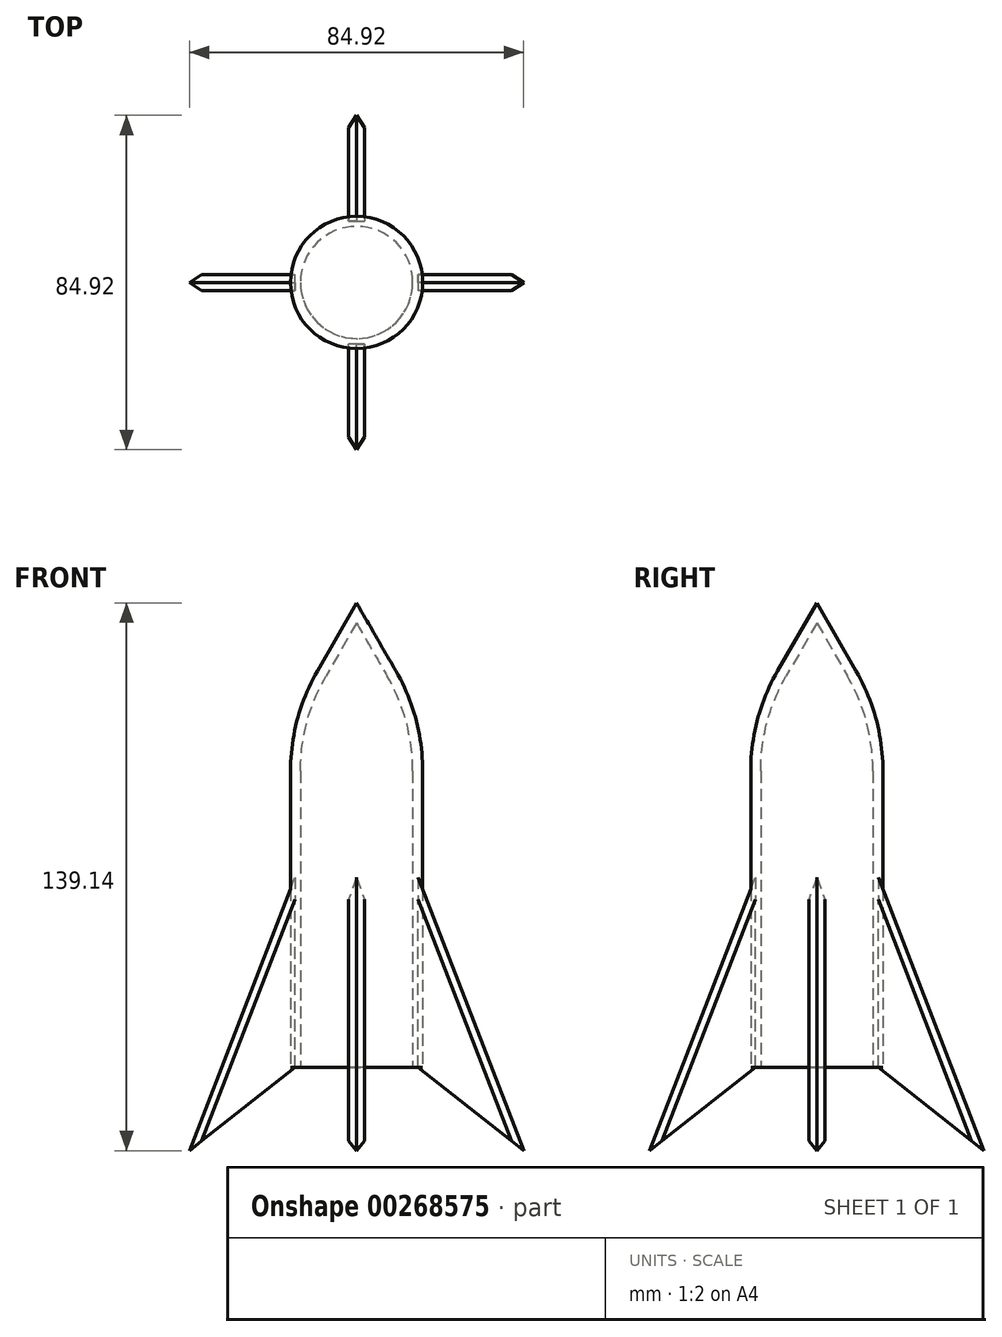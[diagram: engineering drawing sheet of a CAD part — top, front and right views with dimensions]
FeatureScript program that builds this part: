
annotation { "Feature Type Name" : "Feature", "Feature Type Description" : "" }
export const myFeature = defineFeature(function(context is Context, id is Id, definition is map)
    precondition{}
    {
        {
            var Q0;
            Q0=qCreatedBy(makeId("Top.planeOp"),FACE);
            var sketch = newSketch(context, id + "F0", { "sketchPlane" : qUnion([Q0])});
            skCircle(sketch, "E0", {"center": v(0, 0) * mm, "radius": 16.8 * mm});
            skSolve(sketch);
        }
        {
            var Q0;
            Q0=makeQuery(id+"F0.imprint","IMPRINT",FACE,{"disambiguationData":[TD([[makeQuery(id+"F0.imprint","IMPRINT",EDGE,{"derivedFrom":sQuery(id+"F0.wireOp",EDGE,"E0")}),1.0]])]});
            extrude(context, id + "F1", {"entities" : qUnion([Q0]), "depth" : 88.9 * mm});
        }
        {
            var Q0;
            Q0=makeQuery(id+"F1.opExtrude","CAP_FACE",FACE,{"disambiguationData":[OSD([sQuery(id+"F0.wireOp",EDGE,"E0")])],"isStart":false});
            extrude(context, id + "F2", {"entities" : qUnion([Q0]), "operationType" : NewBodyOperationType.ADD, "depth" : 35.56 * mm, "hasDraft" : true, "draftAngle" : 30 * degree, "draftPullDirection" : true});
        }
        {
            var Q0;
            Q0=makeQuery(id+"F2.opExtrude","SWEPT_FACE",FACE,{"disambiguationData":[OSD([sQuery(id+"F0.wireOp",EDGE,"E0")])]});
            fillet(context, id + "F3", {"entities" : qUnion([Q0]), "radius" : 50.8 * mm, "tangentPropagation" : true, "allowEdgeOverflow" : false});
        }
        {
            var Q0;
            Q0=qCreatedBy(makeId("Front.planeOp"),FACE);
            var sketch = newSketch(context, id + "F4", { "sketchPlane" : qUnion([Q0])});
            skLineSegment(sketch, "E1", {"start": v(-15.62, 0) * mm, "end": v(-15.62, 49.74) * mm});
            skLineSegment(sketch, "E2", {"start": v(-15.62, 49.74) * mm, "end": v(-43.24, -21.76) * mm});
            skLineSegment(sketch, "E3", {"start": v(-43.24, -21.76) * mm, "end": v(-15.62, 0) * mm});
            skSolve(sketch);
        }
        {
            var Q0;
            Q0=makeQuery(id+"F4.imprint","IMPRINT",FACE,{"disambiguationData":[TD([[makeQuery(id+"F4.imprint","IMPRINT",EDGE,{"derivedFrom":sQuery(id+"F4.wireOp",EDGE,"E1")}),1.0]])]});
            extrude(context, id + "F5", {"entities" : qUnion([Q0]), "endBound" : BoundingType.SYMMETRIC, "depth" : 4.06 * mm});
        }
        {
            var Q0;
            Q0=makeQuery(id+"F8.opPattern","COPY",EDGE,{"derivedFrom":makeQuery(id+"F5.opExtrude","CAP_EDGE",EDGE,{"disambiguationData":[OSD([sQuery(id+"F4.wireOp",EDGE,"E2")])],"isStart":false}),"instanceName":"2"});
            var Q1;
            Q1=makeQuery(id+"F5.opExtrude","CAP_EDGE",EDGE,{"disambiguationData":[OSD([sQuery(id+"F4.wireOp",EDGE,"E2")])],"isStart":false});
            chamfer(context, id + "F6", {"entities" : qUnion([Q0, Q1]), "width" : 2.54 * mm, "tangentPropagation" : true});
        }
        {
            var Q0;
            Q0=makeQuery(id+"F8.opPattern","COPY",EDGE,{"derivedFrom":makeQuery(id+"F5.opExtrude","CAP_EDGE",EDGE,{"disambiguationData":[OSD([sQuery(id+"F4.wireOp",EDGE,"E2")])],"isStart":true}),"instanceName":"2"});
            var Q1;
            Q1=makeQuery(id+"F5.opExtrude","CAP_EDGE",EDGE,{"disambiguationData":[OSD([sQuery(id+"F4.wireOp",EDGE,"E2")])],"isStart":true});
            chamfer(context, id + "F7", {"entities" : qUnion([Q0, Q1]), "width" : 2.54 * mm, "tangentPropagation" : true});
        }
        {
            var Q0;
            Q0=makeQuery(id+"F5.opExtrude","SWEPT_BODY",BODY,{"disambiguationData":[OSD([sQuery(id+"F4.wireOp",EDGE,"E1"),sQuery(id+"F4.wireOp",EDGE,"E2"),sQuery(id+"F4.wireOp",EDGE,"E3")])]});
            var Q1;
            Q1=makeQuery(id+"F2.opExtrude","SWEPT_FACE",FACE,{"disambiguationData":[OSD([sQuery(id+"F0.wireOp",EDGE,"E0")])]});
            circularPattern(context, id + "F8", {"entities" : qUnion([Q0]), "axis" : qUnion([Q1]), "angle" : 360 * degree, "instanceCount" : 4, "equalSpace" : true});
        }
        {
            var Q0;
            Q0=makeQuery(id+"F1.opExtrude","CAP_FACE",FACE,{"disambiguationData":[OSD([sQuery(id+"F0.wireOp",EDGE,"E0")])],"isStart":true});
            shell(context, id + "F9", {"entities" : qUnion([Q0]), "thickness" : 2.54 * mm});
        }
    });
